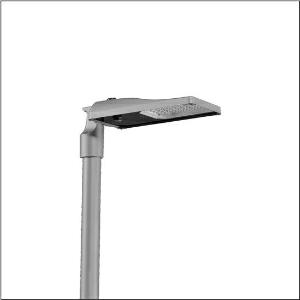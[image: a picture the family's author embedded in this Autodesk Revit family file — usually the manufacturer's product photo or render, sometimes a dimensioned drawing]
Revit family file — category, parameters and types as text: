
# Revit family: streetlight_sl_31_mini___st0_8a_5xh6c31t08ja_3bb2
name_source: partatom
category: Lighting Fixtures
units: mm (PartAtom-declared; Revit-internal decimal feet)

## family parameters
Cut with Voids When Loaded = No
Host = Face
Light Source = No
Part Type = Normal
Room Calculation Point = No
Round Connector Dimension = Use Diameter
Shared = No

## types (1)
- --- (1 x LED, 12270 lm, 82.5 W, 3000K)
    Apparent Load = 83 VA
    CIE Flux Codes = 41 75 97 100 100
    Color Rendering = 70
    Color Temperature = 3000K
    Default Elevation = 1800 mm
    Description = Streetlight SL 31 mini, mast luminaire, primary light control with lens, of PMMA, primary optical cover: cover, of toughened safety glass, transparent, light distribution: ST0.8a, light emission: direct distribution, primary light characteristic: asymmetric, installation type: post-top, side-entry, LED, High Power LED, rated luminous flux: 12.270lm, luminous efficacy: 149lm/W, light colour: 730, colour temperature: 3000K, control: presetting dimming logarithmic, flexible luminous flux parameterisation, time-dependent luminous flux control, constant luminous flux control, power reduction, intelligent temperature release in ECG and LED module, overheat protection, with cable H07RN-F 2x 1.5mm², mains connection: 220..240V, AC, 50/60Hz, connection cable pre-assembled, cable length: 10,5m, start of lifetime: 83W, end of service life: 90W, reduction: 37W, luminaire housing, of diecast aluminium, powder-coated, Siteco® metallic grey (DB 702S), corrosivity category C5 high according to DIN EN ISO 12944, sealing non-destructively replaceable, multi-level sealing system, mast flange (76/60mm) included as standard, inclination: -15°..+20° (post-top) | -20°..+20° (side-entry), adjustable in 5° steps, no sealing on luminaire upper side, Smart Interface below and above, protection rating (complete): IP66, insulation class (complete): insulation class II (safety insulation), certification: CE, ENEC, ENEC+, VDE, UKCA, ZD4i, impact resistance: IK09, permissible operating ambient temperature for outdoor applications: -40..+50°C, standard-compliant lighting for roads and squares, packaging unit: 1 piece

Light Distribution: ST0.8a
    Height = 76 mm
    Lamp = 1 x LED
    Lamp Light Flux = 12270 lm
    Lamp Power = 82.5 W
    Lamp count = 1
    Length = 547 mm
    Luminous efficacy = 149 lm/W
    Manufacturer = Siteco
    ModVariant = No
    Model = 5XH6C31T08JA
    Number of Poles = 1
    OnlyDefault = Yes
    Power Factor = 1
    Product Name = Streetlight SL 31 mini | ST0.8a
    Product group = mast luminaire | pylon top
    ProductGroupID = 6100
    Protection Class = Protection class II
    Protection Degree = IP 66
    RLX_Detail_Level = 1
    RLX_Emergency_Light_Flux = 0 lm
    RLX_Emergency_Type = 0
    RLX_Emergency_Type_DB = No
    RlxData = <blob elided: 40209 chars, md5=30f0a16e>
    Socket = socket
    Standby Power = 0 W
    System Light Flux = 12270 lm
    System Power = 83 W
    Type Comments = factory setting: luminous flux: 100 % | dim-lin: 254 | 870 mA
    Type Image = l_1300332.jpg
    URL = http://relux.com
    VarID = @adj_007111
    Voltage = 0 V
    Weight = 0.00 kg
    Width = 265 mm

## geometry (parser evidence)
native form markers: Blend x4, Sweep x10
no freeform markers — native parametric forms only
